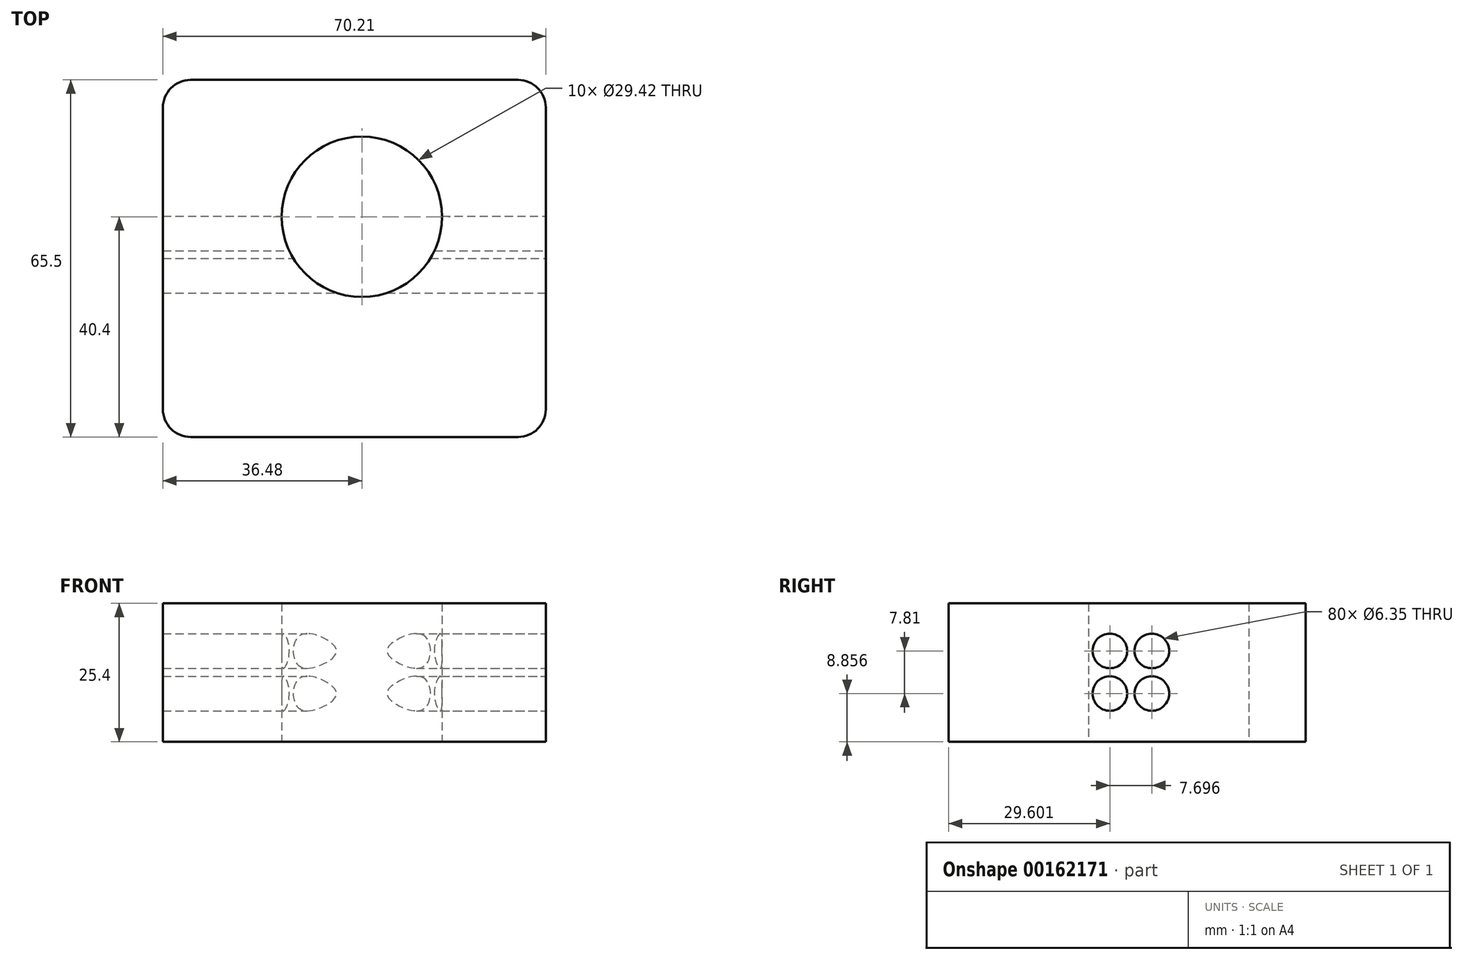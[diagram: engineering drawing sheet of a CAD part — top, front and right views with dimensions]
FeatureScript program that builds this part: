
annotation { "Feature Type Name" : "Feature", "Feature Type Description" : "" }
export const myFeature = defineFeature(function(context is Context, id is Id, definition is map)
    precondition{}
    {
        {
            var Q0;
            Q0=qCreatedBy(makeId("Top.planeOp"),FACE);
            var sketch = newSketch(context, id + "F0", { "sketchPlane" : qUnion([Q0])});
            skLineSegment(sketch, "E0.bottom", {"start": v(-36.48, 25.1) * mm, "end": v(33.73, 25.1) * mm});
            skLineSegment(sketch, "E0.top", {"start": v(-36.48, -40.4) * mm, "end": v(33.73, -40.4) * mm});
            skLineSegment(sketch, "E0.left", {"start": v(-36.48, 25.1) * mm, "end": v(-36.48, -40.4) * mm});
            skLineSegment(sketch, "E0.right", {"start": v(33.73, 25.1) * mm, "end": v(33.73, -40.4) * mm});
            skCircle(sketch, "E1", {"center": v(0, 0) * mm, "radius": 14.71 * mm});
            skSolve(sketch);
        }
        {
            var Q0;
            Q0=makeQuery(id+"F0.imprint","IMPRINT",FACE,{"disambiguationData":[TD([[makeQuery(id+"F0.imprint","IMPRINT",EDGE,{"derivedFrom":sQuery(id+"F0.wireOp",EDGE,"E0.bottom")}),-1.0]])]});
            extrude(context, id + "F1", {"entities" : qUnion([Q0]), "depth" : 25.4 * mm});
        }
        {
            var Q0;
            Q0=makeQuery(id+"F1.opExtrude","SWEPT_EDGE",EDGE,{"disambiguationData":[OSD([sQuery(id+"F0.wireOp",EDGE,"E0.bottom"),sQuery(id+"F0.wireOp",EDGE,"E0.left")])]});
            fillet(context, id + "F2", {"entities" : qUnion([Q0]), "radius" : 5.08 * mm, "tangentPropagation" : true, "allowEdgeOverflow" : false});
        }
        {
            var Q0;
            Q0=makeQuery(id+"F1.opExtrude","SWEPT_EDGE",EDGE,{"disambiguationData":[OSD([sQuery(id+"F0.wireOp",EDGE,"E0.bottom"),sQuery(id+"F0.wireOp",EDGE,"E0.right")])]});
            var Q1;
            Q1=makeQuery(id+"F1.opExtrude","SWEPT_EDGE",EDGE,{"disambiguationData":[OSD([sQuery(id+"F0.wireOp",EDGE,"E0.top"),sQuery(id+"F0.wireOp",EDGE,"E0.right")])]});
            var Q2;
            Q2=makeQuery(id+"F1.opExtrude","SWEPT_EDGE",EDGE,{"disambiguationData":[OSD([sQuery(id+"F0.wireOp",EDGE,"E0.top"),sQuery(id+"F0.wireOp",EDGE,"E0.left")])]});
            fillet(context, id + "F3", {"entities" : qUnion([Q0, Q1, Q2]), "radius" : 5.08 * mm, "tangentPropagation" : true, "allowEdgeOverflow" : false});
        }
        {
            var Q0;
            Q0=makeQuery(id+"F1.opExtrude","SWEPT_FACE",FACE,{"disambiguationData":[OSD([sQuery(id+"F0.wireOp",EDGE,"E0.right")])]});
            var sketch = newSketch(context, id + "F4", { "sketchPlane" : qUnion([Q0])});
            skLineSegment(sketch, "E2.bottom", {"start": v(-3.1, 16.67) * mm, "end": v(-10.8, 16.67) * mm});
            skLineSegment(sketch, "E2.top", {"start": v(-3.1, 8.86) * mm, "end": v(-10.8, 8.86) * mm});
            skLineSegment(sketch, "E2.left", {"start": v(-3.1, 16.67) * mm, "end": v(-3.1, 8.86) * mm});
            skLineSegment(sketch, "E2.right", {"start": v(-10.8, 16.67) * mm, "end": v(-10.8, 8.86) * mm});
            skSolve(sketch);
        }
        {
            var Q0;
            Q0=sQuery(id+"F4.wireOp",VERTEX,"E2.bottom.start");
            var Q1;
            Q1=sQuery(id+"F4.wireOp",VERTEX,"E2.left.end");
            var Q2;
            Q2=sQuery(id+"F4.wireOp",VERTEX,"E2.top.end");
            var Q3;
            Q3=sQuery(id+"F4.wireOp",VERTEX,"E2.right.start");
            var Q4;
            Q4=makeQuery(id+"F1.opExtrude","SWEPT_BODY",BODY,{"disambiguationData":[OSD([sQuery(id+"F0.wireOp",EDGE,"E0.bottom"),sQuery(id+"F0.wireOp",EDGE,"E0.top"),sQuery(id+"F0.wireOp",EDGE,"E0.left"),sQuery(id+"F0.wireOp",EDGE,"E0.right"),sQuery(id+"F0.wireOp",EDGE,"E1")])]});
            hole(context, id + "F5", {"style" : HoleStyle.SIMPLE, "endStyle" : HoleEndStyle.THROUGH, "holeDiameter" : 6.35 * mm, "locations" : qUnion([Q0, Q1, Q2, Q3]), "scope" : qUnion([Q4]), "isTappedThrough" : true});
        }
    });
